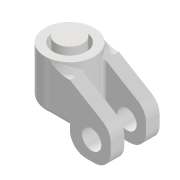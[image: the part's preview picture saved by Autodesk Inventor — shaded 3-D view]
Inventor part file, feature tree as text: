
AUTODESK INVENTOR PART (.ipt)
format: ipt  version: 2022 (Build 260153000, 153)  size: 243,200 bytes
history: native  units: mm
features: extrude x6, sketch x6, fillet x4, projected_geometry x3, plane x1, mirror x1
ambient origin geometry x8: Origin, YZ Plane, XZ Plane, XY Plane, X Axis, Y Axis, Z Axis, Center Point
bodies: Solid1 (feature_tree)
feature tree (21):
  extrude  "Extrusion1"  Depth=12.2mm
  extrude  "Extrusion2"  Depth=3.0mm TaperAngle=0.0deg
  extrude  "Extrusion3"  Depth=3.0mm TaperAngle=0.0deg
  plane  "Work Plane1"
  sketch  "Sketch5"  dims[d11=8.0mm d12=7.0mm d13=7.0mm d14=15.0mm d15=6.0mm]
  extrude  "Extrusion4"  Depth=7.1mm
  mirror  "Mirror2"
  extrude  "Extrusion5"  Depth=7.0mm
  fillet  "Fillet3"  Radius=7.0mm
  fillet  "Fillet5"  Radius=15.0mm
  sketch  "Sketch6"  dims[d16=5.0mm d17=0.0mm d20=100.0mm d21=0.0mm d22=6.0mm d24=3.0mm d28=10.0mm d29=0.0mm d30=2.0mm d31=1.0mm]
  fillet  "Fillet7"  Radius=6.0mm
  extrude  "Extrusion6"  Depth=1.0mm TaperAngle=0.0deg
  fillet  "Fillet6"  Radius=6.0mm
  sketch  "Sketch1"  dims[d0=9.8mm d1=12.2mm]
  sketch  "Sketch2"  dims[d2=3.0mm d3=15.0mm d4=0.0mm]
  projected_geometry  "Projected Loop1"
  sketch  "Sketch3"  dims[d5=2.0mm d6=0.0mm d7=3.0mm d8=0.0mm]
  projected_geometry  "Projected Loop2"
  sketch  "Sketch4"  dims[d9=4.0mm d10=7.1mm]
  projected_geometry  "Projected Loop3"
